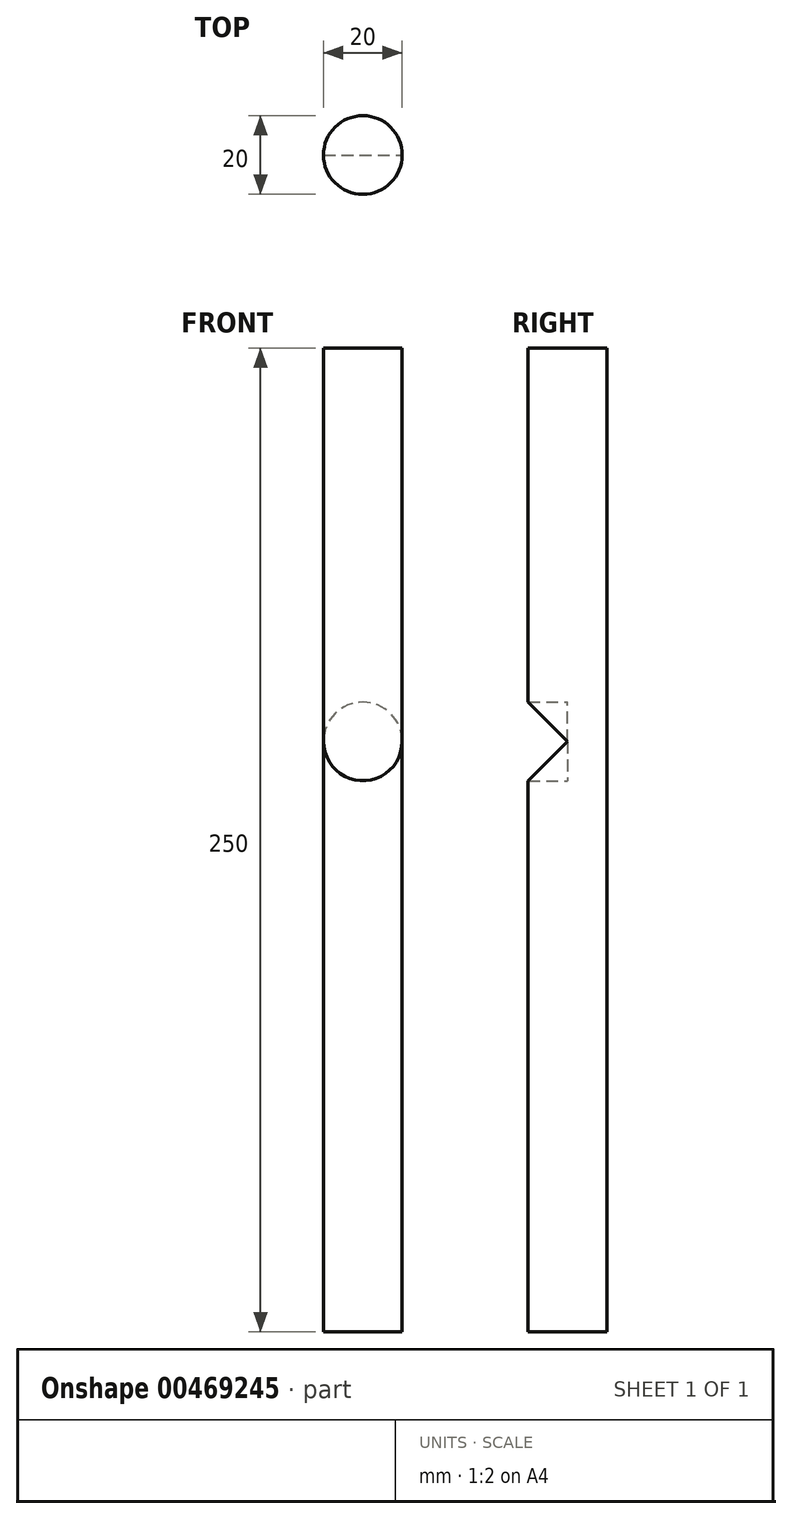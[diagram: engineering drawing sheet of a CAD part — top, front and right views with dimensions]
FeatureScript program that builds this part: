
annotation { "Feature Type Name" : "Feature", "Feature Type Description" : "" }
export const myFeature = defineFeature(function(context is Context, id is Id, definition is map)
    precondition{}
    {
        {
            var Q0;
            Q0=qCreatedBy(makeId("Top.planeOp"),FACE);
            var sketch = newSketch(context, id + "F0", { "sketchPlane" : qUnion([Q0])});
            skCircle(sketch, "E0", {"center": v(0, 0) * mm, "radius": 10 * mm});
            skSolve(sketch);
        }
        {
            var Q0;
            Q0 = qSketchRegion(id + "F0", true);
            extrude(context, id + "F1", {"entities" : qUnion([Q0]), "depth" : 250 * mm});
        }
        {
            var Q0;
            Q0=qCreatedBy(makeId("Front.planeOp"),FACE);
            var sketch = newSketch(context, id + "F2", { "sketchPlane" : qUnion([Q0])});
            skCircle(sketch, "E1", {"center": v(0, 150) * mm, "radius": 10 * mm});
            skSolve(sketch);
        }
        {
            var Q0;
            Q0 = qSketchRegion(id + "F2", true);
            extrude(context, id + "F3", {"entities" : qUnion([Q0]), "operationType" : NewBodyOperationType.REMOVE, "depth" : 10 * mm});
        }
    });
